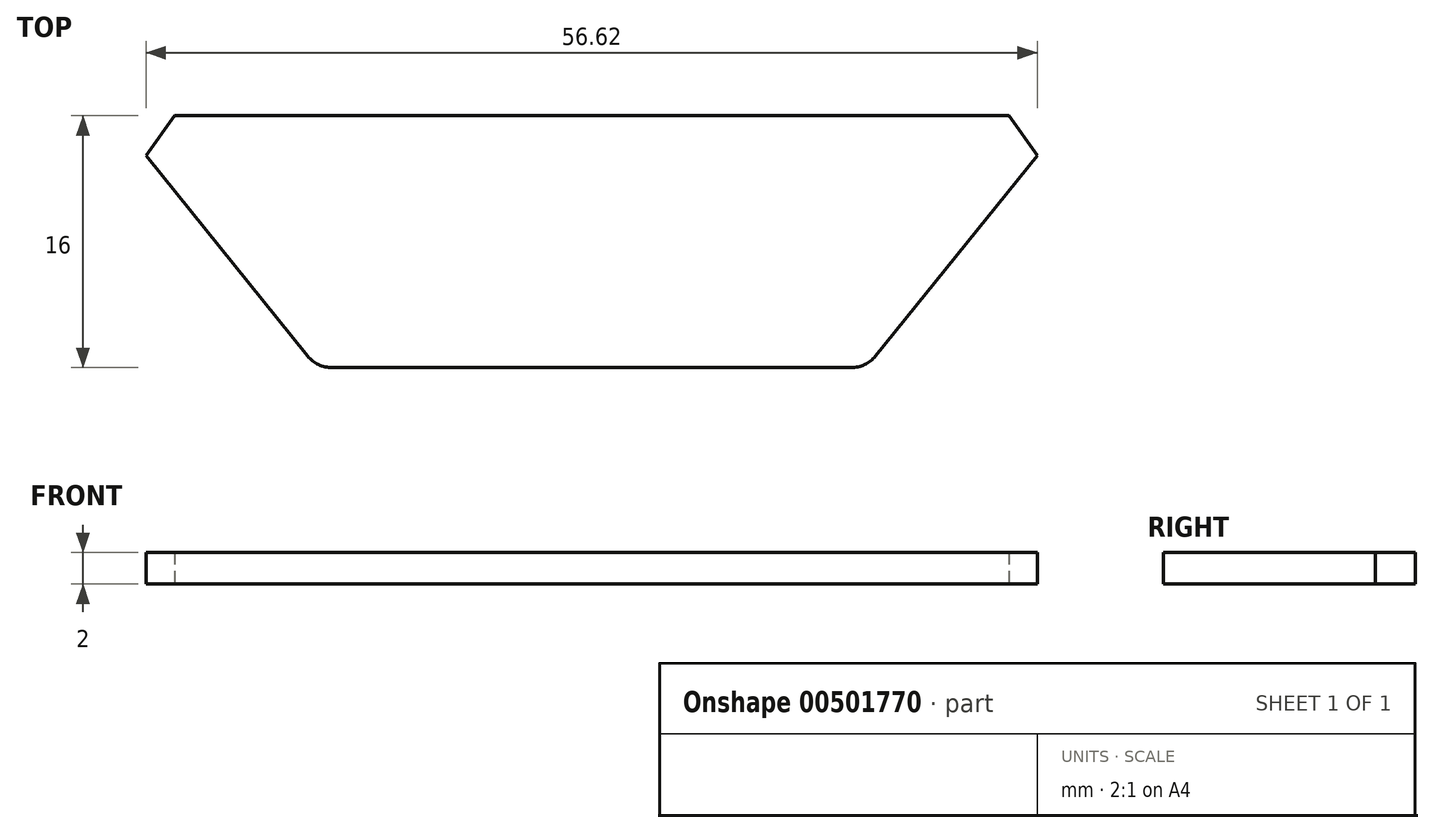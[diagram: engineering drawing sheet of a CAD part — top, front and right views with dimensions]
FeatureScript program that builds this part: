
annotation { "Feature Type Name" : "Feature", "Feature Type Description" : "" }
export const myFeature = defineFeature(function(context is Context, id is Id, definition is map)
    precondition{}
    {
        {
            var Q0;
            Q0=qCreatedBy(makeId("Top.planeOp"),FACE);
            var sketch = newSketch(context, id + "F0", { "sketchPlane" : qUnion([Q0])});
            skLineSegment(sketch, "E0", {"start": v(-31.38, 8.44) * mm, "end": v(-21.1, -4.29) * mm});
            skPoint(sketch, "E1.endSnap0", {"position": v(14.27, -4.84) * mm});
            skLineSegment(sketch, "E2", {"start": v(13.4, -5.03) * mm, "end": v(-19.55, -5.03) * mm});
            skLineSegment(sketch, "E3", {"start": v(25.24, 8.44) * mm, "end": v(14.96, -4.29) * mm});
            skPoint(sketch, "E4.orphan", {"position": v(16.44, -5.03) * mm});
            skLineSegment(sketch, "E5", {"start": v(25.24, 8.44) * mm, "end": v(23.43, 10.97) * mm});
            skLineSegment(sketch, "E6", {"start": v(23.43, 10.97) * mm, "end": v(-29.57, 10.97) * mm});
            skLineSegment(sketch, "E7", {"start": v(-29.57, 10.97) * mm, "end": v(-31.38, 8.44) * mm});
            skPoint(sketch, "E8.visualSharp", {"position": v(-20.5, -5.03) * mm});
            skArc(sketch, "E8.filletArc", {"start": v(-21.1, -4.29) * mm, "mid": v(-20.41, -4.84) * mm, "end": v(-19.55, -5.03) * mm});
            skPoint(sketch, "E9.visualSharp", {"position": v(14.36, -5.03) * mm});
            skArc(sketch, "E9.filletArc", {"start": v(13.4, -5.03) * mm, "mid": v(14.27, -4.84) * mm, "end": v(14.96, -4.29) * mm});
            skSolve(sketch);
        }
        {
            var Q0;
            Q0=makeQuery(id+"F0.imprint","IMPRINT",FACE,{"disambiguationData":[TD([[makeQuery(id+"F0.imprint","IMPRINT",EDGE,{"derivedFrom":sQuery(id+"F0.wireOp",EDGE,"E0")}),1.0]])]});
            extrude(context, id + "F1", {"entities" : qUnion([Q0]), "depth" : 2 * mm});
        }
    });
